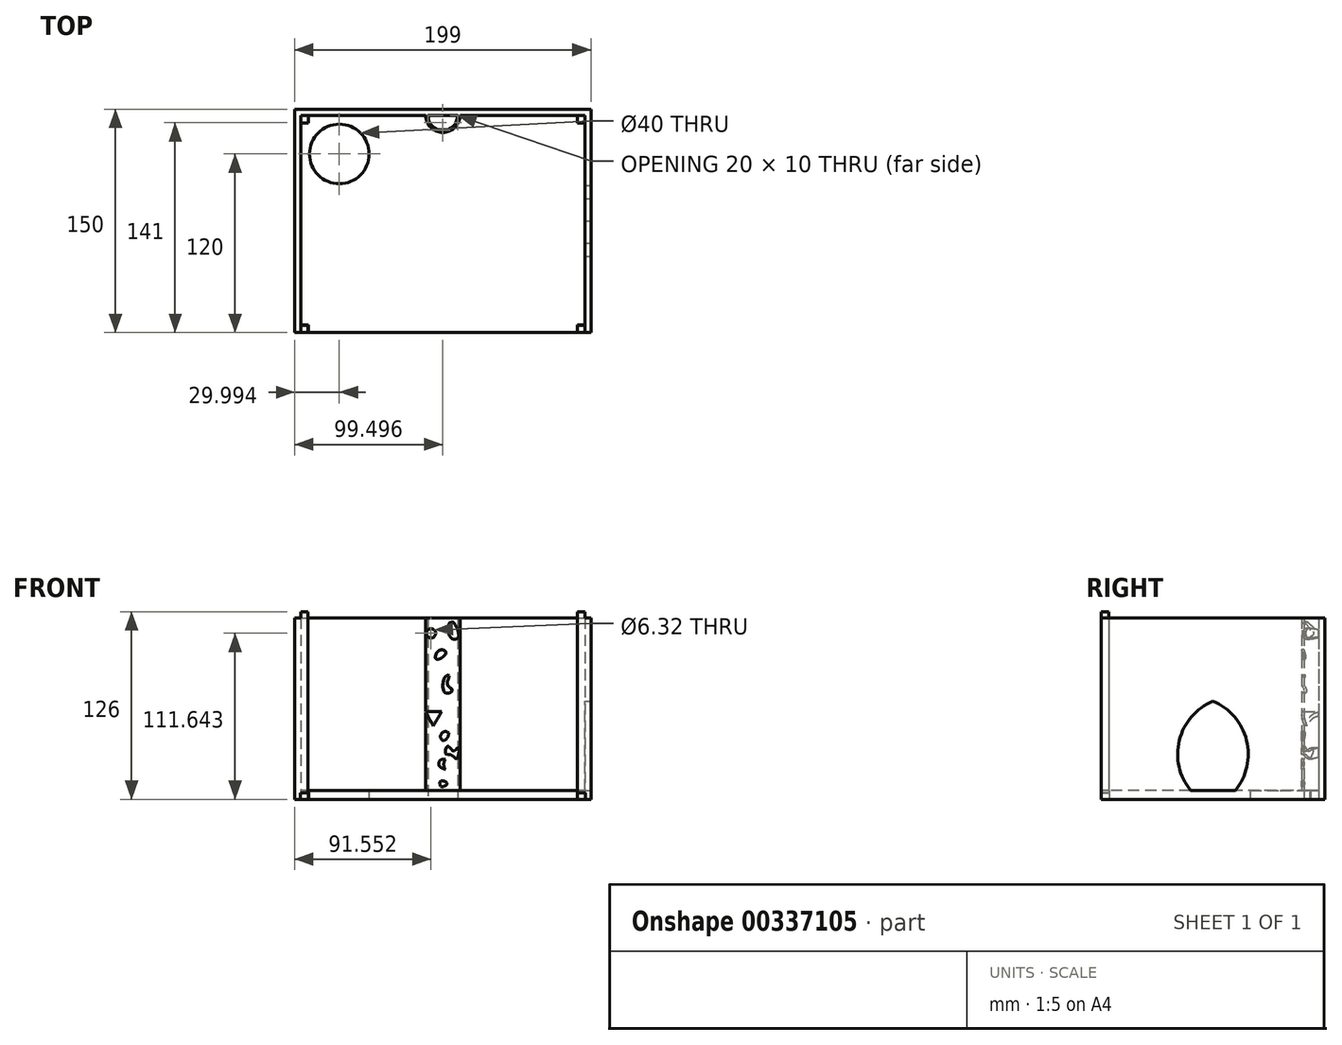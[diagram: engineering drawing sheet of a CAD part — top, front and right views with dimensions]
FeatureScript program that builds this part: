
annotation { "Feature Type Name" : "Feature", "Feature Type Description" : "" }
export const myFeature = defineFeature(function(context is Context, id is Id, definition is map)
    precondition{}
    {
        {
            var Q0;
            Q0=qCreatedBy(makeId("Top.planeOp"),FACE);
            var sketch = newSketch(context, id + "F0", { "sketchPlane" : qUnion([Q0])});
            skLineSegment(sketch, "E0.bottom", {"start": v(-134.21, 150) * mm, "end": v(64.79, 150) * mm});
            skLineSegment(sketch, "E0.left", {"start": v(-134.21, 150) * mm, "end": v(-134.21, 0) * mm});
            skLineSegment(sketch, "E0.right", {"start": v(64.79, 150) * mm, "end": v(64.79, 90) * mm});
            skLineSegment(sketch, "E1.0", {"start": v(60.79, 146) * mm, "end": v(60.79, 90) * mm});
            skLineSegment(sketch, "E1.1", {"start": v(-130.21, 146) * mm, "end": v(60.79, 146) * mm});
            skLineSegment(sketch, "E1.2", {"start": v(-130.21, 146) * mm, "end": v(-130.21, 0) * mm});
            skLineSegment(sketch, "E2", {"start": v(-134.21, 0) * mm, "end": v(-130.21, 0) * mm});
            skLineSegment(sketch, "E3", {"start": v(60.79, 0) * mm, "end": v(64.79, 0) * mm});
            skLineSegment(sketch, "E4.bottom", {"start": v(-130.21, 146) * mm, "end": v(-125.21, 146) * mm});
            skLineSegment(sketch, "E4.top", {"start": v(-130.21, 141) * mm, "end": v(-125.21, 141) * mm});
            skLineSegment(sketch, "E4.left", {"start": v(-130.21, 146) * mm, "end": v(-130.21, 141) * mm});
            skLineSegment(sketch, "E4.right", {"start": v(-125.21, 146) * mm, "end": v(-125.21, 141) * mm});
            skLineSegment(sketch, "E5.bottom", {"start": v(60.79, 146) * mm, "end": v(55.79, 146) * mm});
            skLineSegment(sketch, "E5.top", {"start": v(60.79, 141) * mm, "end": v(55.79, 141) * mm});
            skLineSegment(sketch, "E5.left", {"start": v(60.79, 146) * mm, "end": v(60.79, 141) * mm});
            skLineSegment(sketch, "E5.right", {"start": v(55.79, 146) * mm, "end": v(55.79, 141) * mm});
            skLineSegment(sketch, "E6.bottom", {"start": v(60.79, 0) * mm, "end": v(55.79, 0) * mm});
            skLineSegment(sketch, "E6.top", {"start": v(60.79, 5) * mm, "end": v(55.79, 5) * mm});
            skLineSegment(sketch, "E6.left", {"start": v(60.79, 0) * mm, "end": v(60.79, 5) * mm});
            skLineSegment(sketch, "E6.right", {"start": v(55.79, 0) * mm, "end": v(55.79, 5) * mm});
            skLineSegment(sketch, "E7.bottom", {"start": v(-130.21, 0) * mm, "end": v(-125.21, 0) * mm});
            skLineSegment(sketch, "E7.top", {"start": v(-130.21, 5) * mm, "end": v(-125.21, 5) * mm});
            skLineSegment(sketch, "E7.left", {"start": v(-130.21, 0) * mm, "end": v(-130.21, 5) * mm});
            skLineSegment(sketch, "E7.right", {"start": v(-125.21, 0) * mm, "end": v(-125.21, 5) * mm});
            skArc(sketch, "E8", {"start": v(-44.71, 146) * mm, "mid": v(-34.71, 136) * mm, "end": v(-24.71, 146) * mm});
            skLineSegment(sketch, "E9.trimOffspring", {"start": v(64.79, 60) * mm, "end": v(64.79, 0) * mm});
            skLineSegment(sketch, "E10.trimOffspring", {"start": v(60.79, 60) * mm, "end": v(60.79, 0) * mm});
            skLineSegment(sketch, "E11", {"start": v(64.79, 90) * mm, "end": v(64.79, 60) * mm});
            skLineSegment(sketch, "E12", {"start": v(60.79, 90) * mm, "end": v(60.79, 60) * mm});
            skArc(sketch, "E13.trimOffspring", {"start": v(-46.21, 146) * mm, "mid": v(-34.71, 134.5) * mm, "end": v(-23.21, 146) * mm});
            skSolve(sketch);
        }
        {
            var Q0;
            Q0=makeQuery(id+"F0.imprint","IMPRINT",FACE,{"disambiguationData":[TD([[makeQuery(id+"F0.imprint","IMPRINT",EDGE,{"derivedFrom":sQuery(id+"F0.wireOp",EDGE,"E0.bottom")}),-1.0]])]});
            var Q1;
            {var subQ0=sQuery(id+"F0.wireOp",EDGE,"E8");Q1=makeQuery(id+"F0.imprint","IMPRINT",FACE,{"disambiguationData":[TD([[makeQuery(id+"F0.imprint","IMPRINT",EDGE,{"derivedFrom":subQ0}),-1.0]])]});}
            extrude(context, id + "F1", {"entities" : qUnion([Q0, Q1]), "depth" : 122 * mm, "offsetDistance" : 25 * mm});
        }
        {
            var Q0;
            Q0=makeQuery(id+"F0.imprint","IMPRINT",FACE,{"disambiguationData":[TD([[makeQuery(id+"F0.imprint","IMPRINT",EDGE,{"derivedFrom":sQuery(id+"F0.wireOp",EDGE,"E4.bottom")}),-1.0]])]});
            var Q1;
            Q1=makeQuery(id+"F0.imprint","IMPRINT",FACE,{"disambiguationData":[TD([[makeQuery(id+"F0.imprint","IMPRINT",EDGE,{"derivedFrom":sQuery(id+"F0.wireOp",EDGE,"E7.bottom")}),1.0]])]});
            var Q2;
            Q2=makeQuery(id+"F0.imprint","IMPRINT",FACE,{"disambiguationData":[TD([[makeQuery(id+"F0.imprint","IMPRINT",EDGE,{"derivedFrom":sQuery(id+"F0.wireOp",EDGE,"E6.bottom")}),-1.0]])]});
            var Q3;
            Q3=makeQuery(id+"F0.imprint","IMPRINT",FACE,{"disambiguationData":[TD([[makeQuery(id+"F0.imprint","IMPRINT",EDGE,{"derivedFrom":sQuery(id+"F0.wireOp",EDGE,"E5.bottom")}),1.0]])]});
            extrude(context, id + "F2", {"entities" : qUnion([Q0, Q1, Q2, Q3]), "operationType" : NewBodyOperationType.ADD, "depth" : 126 * mm, "offsetDistance" : 25 * mm});
        }
        {
            var Q0;
            Q0=makeQuery(id+"F0.imprint","IMPRINT",FACE,{"disambiguationData":[TD([[makeQuery(id+"F0.imprint","IMPRINT",EDGE,{"derivedFrom":sQuery(id+"F0.wireOp",EDGE,"E0.bottom")}),-1.0]])]});
            var sketch = newSketch(context, id + "F3", { "sketchPlane" : qUnion([Q0])});
            skLineSegment(sketch, "E14.bottom", {"start": v(-134.22, 0) * mm, "end": v(64.79, 0) * mm});
            skLineSegment(sketch, "E14.top", {"start": v(-134.22, 150) * mm, "end": v(64.79, 150) * mm});
            skLineSegment(sketch, "E14.left", {"start": v(-134.22, 0) * mm, "end": v(-134.22, 150) * mm});
            skLineSegment(sketch, "E14.right", {"start": v(64.79, 0) * mm, "end": v(64.79, 150) * mm});
            skLineSegment(sketch, "E15", {"start": v(-134.22, 150) * mm, "end": v(-104.22, 150) * mm});
            skPoint(sketch, "E16", {"position": v(-104.22, 120) * mm});
            skCircle(sketch, "E17", {"center": v(-104.22, 120) * mm, "radius": 20 * mm});
            skPoint(sketch, "E18.orphan", {"position": v(64.79, 146) * mm});
            skPoint(sketch, "E19.orphan", {"position": v(-134.22, 146) * mm});
            skPoint(sketch, "E20.center.orphan", {"position": v(-34.71, 146) * mm});
            skArc(sketch, "E21", {"start": v(-44.71, 146) * mm, "mid": v(-34.71, 136) * mm, "end": v(-24.71, 146) * mm});
            skLineSegment(sketch, "E22", {"start": v(-24.71, 146) * mm, "end": v(-44.71, 146) * mm});
            skLineSegment(sketch, "E23", {"start": v(55.78, 5.25) * mm, "end": v(55.53, 5.25) * mm});
            skLineSegment(sketch, "E24.bottom", {"start": v(55.78, 5.25) * mm, "end": v(61.08, 5.25) * mm});
            skLineSegment(sketch, "E24.left", {"start": v(55.53, 5.25) * mm, "end": v(55.53, 0) * mm});
            skLineSegment(sketch, "E24.right", {"start": v(61.08, 5.25) * mm, "end": v(61.08, 0) * mm});
            skLineSegment(sketch, "E25.bottom", {"start": v(-124.94, 5.24) * mm, "end": v(-130.46, 5.24) * mm});
            skLineSegment(sketch, "E25.left", {"start": v(-124.94, 5.24) * mm, "end": v(-124.94, 0) * mm});
            skLineSegment(sketch, "E25.right", {"start": v(-130.46, 5.24) * mm, "end": v(-130.46, 0) * mm});
            skLineSegment(sketch, "E26", {"start": v(-125.21, 140.74) * mm, "end": v(-124.96, 140.74) * mm});
            skLineSegment(sketch, "E27.bottom", {"start": v(-124.96, 140.74) * mm, "end": v(-130.48, 140.74) * mm});
            skLineSegment(sketch, "E27.top", {"start": v(-124.96, 146.29) * mm, "end": v(-130.48, 146.29) * mm});
            skLineSegment(sketch, "E27.left", {"start": v(-124.96, 140.74) * mm, "end": v(-124.96, 146.29) * mm});
            skLineSegment(sketch, "E27.right", {"start": v(-130.48, 140.74) * mm, "end": v(-130.48, 146.29) * mm});
            skLineSegment(sketch, "E28", {"start": v(55.79, 140.75) * mm, "end": v(55.54, 140.75) * mm});
            skLineSegment(sketch, "E29.bottom", {"start": v(55.54, 140.75) * mm, "end": v(61.1, 140.75) * mm});
            skLineSegment(sketch, "E29.top", {"start": v(55.54, 146.25) * mm, "end": v(61.1, 146.25) * mm});
            skLineSegment(sketch, "E29.left", {"start": v(55.54, 140.75) * mm, "end": v(55.54, 146.25) * mm});
            skLineSegment(sketch, "E29.right", {"start": v(61.1, 140.75) * mm, "end": v(61.1, 146.25) * mm});
            skLineSegment(sketch, "E30", {"start": v(55.53, 0) * mm, "end": v(61.08, 0) * mm});
            skLineSegment(sketch, "E31", {"start": v(55.8, 0) * mm, "end": v(60.8, 0) * mm});
            skLineSegment(sketch, "E32", {"start": v(55.8, 0) * mm, "end": v(55.53, 0) * mm});
            skLineSegment(sketch, "E33", {"start": v(60.8, 0) * mm, "end": v(61.08, 0) * mm});
            skSolve(sketch);
        }
        {
            var Q0;
            {var subQ14=sQuery(id+"F3.wireOp",EDGE,"E14.top");Q0=makeQuery(id+"F3.imprint","IMPRINT",FACE,{"disambiguationData":[TD([[makeQuery(id+"F3.imprint","IMPRINT",EDGE,{"derivedFrom":subQ14}),-1.0]])]});}
            var Q1;
            {var subQ8=makeQuery(id+"F0.imprint","IMPRINT",EDGE,{"derivedFrom":sQuery(id+"F0.wireOp",EDGE,"E7.left")});Q1=makeQuery(id+"F3.imprint","IMPRINT",FACE,{"disambiguationData":[TD([[makeQuery(id+"F3.imprint","IMPRINT",EDGE,{"derivedFrom":subQ8}),-1.0]])]});}
            var Q2;
            Q2=makeQuery(id+"F3.imprint","IMPRINT",FACE,{"disambiguationData":[TD([[makeQuery(id+"F3.imprint","IMPRINT",EDGE,{"derivedFrom":sQuery(id+"F3.wireOp",EDGE,"E17")}),-1.0]])]});
            var Q3;
            {var subQ5=makeQuery(id+"F0.imprint","IMPRINT",EDGE,{"derivedFrom":sQuery(id+"F0.wireOp",EDGE,"E7.left")});Q3=makeQuery(id+"F3.imprint","IMPRINT",FACE,{"disambiguationData":[TD([[makeQuery(id+"F3.imprint","IMPRINT",EDGE,{"derivedFrom":subQ5}),1.0]])]});}
            var Q4;
            {var subQ1=sQuery(id+"F3.wireOp",EDGE,"E24.bottom");var subQ5=makeQuery(id+"F3.imprint","IMPRINT",VERTEX,{"derivedFrom":subQ1});Q4=makeQuery(id+"F3.imprint","IMPRINT",FACE,{"disambiguationData":[TD([[makeQuery(id+"F3.imprint","IMPRINT",EDGE,{"disambiguationData":[TD([[subQ5,1.0]])],"derivedFrom":subQ1}),-1.0]])]});}
            var Q5;
            {var subQ3=sQuery(id+"F3.wireOp",EDGE,"E24.right");var subQ4=sQuery(id+"F3.wireOp",EDGE,"E24.bottom");var subQ5=makeQuery(id+"F3.imprint","INTERSECT",VERTEX,{"derivedFrom":[subQ4,subQ3]});Q5=makeQuery(id+"F3.imprint","IMPRINT",FACE,{"disambiguationData":[TD([[makeQuery(id+"F3.imprint","IMPRINT",EDGE,{"disambiguationData":[TD([[subQ5,-1.0]])],"derivedFrom":subQ3}),-1.0]])]});}
            var Q6;
            Q6=makeQuery(id+"F0.imprint","IMPRINT",FACE,{"disambiguationData":[TD([[makeQuery(id+"F0.imprint","IMPRINT",EDGE,{"derivedFrom":sQuery(id+"F0.wireOp",EDGE,"E5.bottom")}),1.0]])]});
            var Q7;
            {var subQ0=sQuery(id+"F0.wireOp",EDGE,"E5.bottom");var subQ1=makeQuery(id+"F0.imprint","IMPRINT",EDGE,{"derivedFrom":subQ0});Q7=makeQuery(id+"F3.imprint","IMPRINT",FACE,{"disambiguationData":[TD([[makeQuery(id+"F3.imprint","IMPRINT",EDGE,{"derivedFrom":subQ1}),1.0]])]});}
            var Q8;
            {var subQ2=sQuery(id+"F3.wireOp",EDGE,"E29.top");Q8=makeQuery(id+"F3.imprint","IMPRINT",FACE,{"disambiguationData":[TD([[makeQuery(id+"F3.imprint","IMPRINT",EDGE,{"derivedFrom":subQ2}),-1.0]])]});}
            var Q9;
            Q9=makeQuery(id+"F0.imprint","IMPRINT",FACE,{"disambiguationData":[TD([[makeQuery(id+"F0.imprint","IMPRINT",EDGE,{"derivedFrom":sQuery(id+"F0.wireOp",EDGE,"E4.bottom")}),-1.0]])]});
            var Q10;
            {var subQ0=sQuery(id+"F0.wireOp",EDGE,"E4.bottom");var subQ1=makeQuery(id+"F0.imprint","IMPRINT",EDGE,{"derivedFrom":subQ0});Q10=makeQuery(id+"F3.imprint","IMPRINT",FACE,{"disambiguationData":[TD([[makeQuery(id+"F3.imprint","IMPRINT",EDGE,{"derivedFrom":subQ1}),-1.0]])]});}
            var Q11;
            Q11=makeQuery(id+"F0.imprint","IMPRINT",FACE,{"disambiguationData":[TD([[makeQuery(id+"F0.imprint","IMPRINT",EDGE,{"derivedFrom":sQuery(id+"F0.wireOp",EDGE,"E0.bottom")}),-1.0]])]});
            extrude(context, id + "F4", {"entities" : qUnion([Q0, Q1, Q2, Q3, Q4, Q5, Q6, Q7, Q8, Q9, Q10, Q11]), "operationType" : NewBodyOperationType.ADD, "depth" : 6 * mm, "offsetDistance" : 25 * mm});
        }
        {
            var Q0;
            Q0=qCreatedBy(makeId("Top.planeOp"),FACE);
            var sketch = newSketch(context, id + "F5", { "sketchPlane" : qUnion([Q0])});
            skLineSegment(sketch, "E34", {"start": v(-44.7, 146) * mm, "end": v(-24.73, 146) * mm});
            skArc(sketch, "E35", {"start": v(-44.7, 146) * mm, "mid": v(-34.71, 136.02) * mm, "end": v(-24.73, 146) * mm});
            skSolve(sketch);
        }
        {
            var Q0;
            Q0 = qSketchRegion(id + "F5", true);
            extrude(context, id + "F6", {"entities" : qUnion([Q0]), "operationType" : NewBodyOperationType.REMOVE, "depth" : 174 * mm, "offsetDistance" : 25 * mm});
        }
        {
            var Q0;
            Q0=makeQuery(id+"F1.opExtrude","SWEPT_FACE",FACE,{"disambiguationData":[OSD([sQuery(id+"F0.wireOp",EDGE,"E0.right"),sQuery(id+"F0.wireOp",EDGE,"E9.trimOffspring"),sQuery(id+"F0.wireOp",EDGE,"E11")])]});
            var sketch = newSketch(context, id + "F7", { "sketchPlane" : qUnion([Q0])});
            skLineSegment(sketch, "E36", {"start": v(75, 6) * mm, "end": v(90, 6) * mm});
            skArc(sketch, "E37", {"start": v(90, 6) * mm, "mid": v(97.57, 39.77) * mm, "end": v(75, 66) * mm});
            skArc(sketch, "E38.MirrorCS", {"start": v(60, 6) * mm, "mid": v(52.43, 39.77) * mm, "end": v(75, 66) * mm});
            skLineSegment(sketch, "E39.MirrorCS", {"start": v(75, 6) * mm, "end": v(60, 6) * mm});
            skSolve(sketch);
        }
        {
            var Q0;
            Q0=makeQuery(id+"F7.imprint","IMPRINT",FACE,{"disambiguationData":[TD([[makeQuery(id+"F7.imprint","IMPRINT",EDGE,{"derivedFrom":sQuery(id+"F7.wireOp",EDGE,"E36")}),1.0]])]});
            extrude(context, id + "F8", {"entities" : qUnion([Q0]), "operationType" : NewBodyOperationType.REMOVE, "oppositeDirection" : true, "depth" : 4 * mm, "offsetDistance" : 25 * mm});
        }
        {
            var Q0;
            {var subQ2=sQuery(id+"F3.wireOp",EDGE,"E14.left");Q0=makeQuery(id+"F3.imprint","IMPRINT",FACE,{"disambiguationData":[TD([[makeQuery(id+"F3.imprint","IMPRINT",EDGE,{"derivedFrom":subQ2}),-1.0]])]});}
            var Q1;
            Q1=makeQuery(id+"F3.imprint","IMPRINT",FACE,{"disambiguationData":[TD([[makeQuery(id+"F3.imprint","IMPRINT",EDGE,{"derivedFrom":sQuery(id+"F3.wireOp",EDGE,"E14.right")}),1.0]])]});
            var Q2;
            {var subQ0=sQuery(id+"F3.wireOp",EDGE,"E25.left");Q2=makeQuery(id+"F3.imprint","IMPRINT",FACE,{"disambiguationData":[TD([[makeQuery(id+"F3.imprint","IMPRINT",EDGE,{"derivedFrom":subQ0}),-1.0]])]});}
            var Q3;
            {var subQ0=sQuery(id+"F3.wireOp",EDGE,"E25.right");Q3=makeQuery(id+"F3.imprint","IMPRINT",FACE,{"disambiguationData":[TD([[makeQuery(id+"F3.imprint","IMPRINT",EDGE,{"derivedFrom":subQ0}),1.0]])]});}
            var Q4;
            {var subQ6=sQuery(id+"F3.wireOp",EDGE,"E23");Q4=makeQuery(id+"F3.imprint","IMPRINT",FACE,{"disambiguationData":[TD([[makeQuery(id+"F3.imprint","IMPRINT",EDGE,{"derivedFrom":subQ6}),1.0]])]});}
            var Q5;
            {var subQ1=sQuery(id+"F3.wireOp",EDGE,"E24.right");Q5=makeQuery(id+"F3.imprint","IMPRINT",FACE,{"disambiguationData":[TD([[makeQuery(id+"F3.imprint","IMPRINT",EDGE,{"derivedFrom":subQ1}),-1.0]])]});}
            var Q6;
            Q6=makeQuery(id+"F0.imprint","IMPRINT",FACE,{"disambiguationData":[TD([[makeQuery(id+"F0.imprint","IMPRINT",EDGE,{"derivedFrom":sQuery(id+"F0.wireOp",EDGE,"E5.bottom")}),1.0]])]});
            var Q7;
            {var subQ0=sQuery(id+"F0.wireOp",EDGE,"E4.bottom");var subQ1=makeQuery(id+"F0.imprint","IMPRINT",EDGE,{"derivedFrom":subQ0});Q7=makeQuery(id+"F3.imprint","IMPRINT",FACE,{"disambiguationData":[TD([[makeQuery(id+"F3.imprint","IMPRINT",EDGE,{"derivedFrom":subQ1}),-1.0]])]});}
            extrude(context, id + "F9", {"entities" : qUnion([Q0, Q1, Q2, Q3, Q4, Q5, Q6, Q7]), "operationType" : NewBodyOperationType.REMOVE, "depth" : 4.5 * mm, "offsetDistance" : 25 * mm});
        }
        {
            var Q0;
            Q0=qCreatedBy(makeId("Front.planeOp"),FACE);
            var sketch = newSketch(context, id + "F10", { "sketchPlane" : qUnion([Q0])});
            skCircle(sketch, "E40", {"center": v(-42.66, 111.64) * mm, "radius": 3.16 * mm});
            skCircle(sketch, "E41.cCircle", {"center": v(-41.06, 55.78) * mm, "radius": 3.2 * mm, "construction": true});
            skLineSegment(sketch, "E41.0", {"start": v(-46.6, 58.98) * mm, "end": v(-35.53, 58.98) * mm});
            skLineSegment(sketch, "E41.1", {"start": v(-35.53, 58.98) * mm, "end": v(-41.06, 49.4) * mm});
            skLineSegment(sketch, "E41.2", {"start": v(-41.06, 49.4) * mm, "end": v(-46.6, 58.98) * mm});
            skPoint(sketch, "E41.0.midPoint", {"position": v(-41.06, 58.98) * mm});
            skArc(sketch, "E42", {"start": v(-35.5, 26.83) * mm, "mid": v(-37.44, 23.98) * mm, "end": v(-35.5, 21.13) * mm});
            skLineSegment(sketch, "E43", {"start": v(-35.5, 21.13) * mm, "end": v(-33.04, 20.19) * mm});
            skLineSegment(sketch, "E44", {"start": v(-33.04, 26.83) * mm, "end": v(-35.5, 26.83) * mm});
            skArc(sketch, "E45", {"start": v(-33.04, 26.83) * mm, "mid": v(-34.05, 23.5) * mm, "end": v(-33.04, 20.19) * mm});
            skArc(sketch, "E46", {"start": v(-30.82, 44.84) * mm, "mid": v(-35.76, 44.1) * mm, "end": v(-34.32, 39.3) * mm});
            skArc(sketch, "E47", {"start": v(-34.32, 39.3) * mm, "mid": v(-31.63, 41.48) * mm, "end": v(-30.82, 44.84) * mm});
            skFitSpline(sketch, "E48", {"points": [v(-29.58, 30.05) * mm, v(-25.18, 27.46) * mm, v(-24.28, 34.68) * mm, v(-27.44, 32.42) * mm, v(-31.39, 35.92) * mm, v(-32.74, 30.5) * mm, v(-29.58, 30.05) * mm]});
            skFitSpline(sketch, "E49", {"points": [v(-36.24, 12.22) * mm, v(-35.79, 8.72) * mm, v(-31.84, 10.76) * mm, v(-36.24, 12.22) * mm]});
            skFitSpline(sketch, "E50", {"points": [v(-30.3, 83.16) * mm, v(-31.74, 77.39) * mm, v(-28.39, 73.23) * mm, v(-33.04, 71.62) * mm, v(-33.04, 82.35) * mm, v(-30.3, 83.16) * mm]});
            skFitSpline(sketch, "E51", {"points": [v(-37.07, 100.15) * mm, v(-39.22, 94.25) * mm, v(-32.74, 98.27) * mm, v(-37.07, 100.15) * mm]});
            skFitSpline(sketch, "E52", {"points": [v(-29.06, 119.47) * mm, v(-29.86, 109.1) * mm, v(-24.27, 109.1) * mm, v(-29.06, 119.47) * mm]});
            skSolve(sketch);
        }
        {
            var Q0;
            Q0 = qSketchRegion(id + "F10", true);
            extrude(context, id + "F11", {"entities" : qUnion([Q0]), "operationType" : NewBodyOperationType.REMOVE, "oppositeDirection" : true, "depth" : 146 * mm, "offsetDistance" : 25 * mm, "hasSecondDirection" : true, "secondDirectionOppositeDirection" : true, "secondDirectionDepth" : 82.1 * mm});
        }
    });
